# Revit family: HeartFelt-Linear-Endcap Panel1_HunterDouglasEurope
name_source: partatom
category: Specialty Equipment
revit_build: Autodesk Revit 2016 (Build: 20150220_1215(x64)
units: mm (PartAtom-declared; Revit-internal decimal feet)

## family parameters
Always vertical = Yes
Cut with Voids When Loaded = No
OmniClass Number = 23.35.70.24.11.17.14
OmniClass Title = Linear Ceilings
Part Type = Normal
Room Calculation Point = No
Round Connector Dimension = Use Diameter
Shared = No
Work Plane-Based = No

## types (36) — shared parameters
EN13501-1_Fire rating = Class B,s1,d0
Manufacturer = Hunter Douglas
Product Data = http://assets2.hunterdouglascontract.com
Product Line = HeartFelt® Linear
Subcategory = HeartFelt® Ceilings
Thickness = 6 mm  [stored 0.019685 ft]
URL = http://www.hunterdouglasarchitectural.eu

## per-type parameters (varying)
| type | Article Code | Colour Code | Height | Material | Model |
| Endcap Panel1_40x55_7575 Creme | 38.4208 | 7575 | 51.5 mm  [stored 0.168963 ft] | HeartFelt-7575-Creme_HunterDouglasEurope | HeartFelt EndcapPanel1 40x55 |
| Endcap Panel1_40x55_7576 Light Brown | 38.4208 | 7576 | 51.5 mm  [stored 0.168963 ft] | HeartFelt-7576-Light Brown_HunterDouglasEurope | HeartFelt EndcapPanel1 40x55 |
| Endcap Panel1_40x55_7577 Medium Brown | 38.4208 | 7577 | 51.5 mm  [stored 0.168963 ft] | HeartFelt-7577-Medium Brown_HunterDouglasEurope | HeartFelt EndcapPanel1 40x55 |
| Endcap Panel1_40x55_7578 Dark Brown | 38.4208 | 7578 | 51.5 mm  [stored 0.168963 ft] | HeartFelt-7578-Dark Brown_HunterDouglasEurope | HeartFelt EndcapPanel1 40x55 |
| Endcap Panel1_40x55_7579 Umber | 38.4208 | 7579 | 51.5 mm  [stored 0.168963 ft] | HeartFelt-7579-Umber_HunterDouglasEurope | HeartFelt EndcapPanel1 40x55 |
| Endcap Panel1_40x55_7593 White | 38.4208 | 7593 | 51.5 mm  [stored 0.168963 ft] | HeartFelt-7593-White_HunterDouglasEurope | HeartFelt EndcapPanel1 40x55 |
| Endcap Panel1_40x55_7594 Black | 38.4208 | 7594 | 51.5 mm  [stored 0.168963 ft] | HeartFelt-7594-Black_HunterDouglasEurope | HeartFelt EndcapPanel1 40x55 |
| Endcap Panel1_40x55_7595 Off White | 38.4208 | 7595 | 51.5 mm  [stored 0.168963 ft] | HeartFelt-7595-Off White_HunterDouglasEurope | HeartFelt EndcapPanel1 40x55 |
| Endcap Panel1_40x55_7596 Light Grey | 38.4208 | 7596 | 51.5 mm  [stored 0.168963 ft] | HeartFelt-7596-Light Grey_HunterDouglasEurope | HeartFelt EndcapPanel1 40x55 |
| Endcap Panel1_40x55_7597 Middle Grey | 38.4208 | 7597 | 51.5 mm  [stored 0.168963 ft] | HeartFelt-7597-Middle Grey_HunterDouglasEurope | HeartFelt EndcapPanel1 40x55 |
| Endcap Panel1_40x55_7598 Dark Grey | 38.4208 | 7598 | 51.5 mm  [stored 0.168963 ft] | HeartFelt-7598-Dark Grey_HunterDouglasEurope | HeartFelt EndcapPanel1 40x55 |
| Endcap Panel1_40x55_7599 Anthracite | 38.4208 | 7599 | 51.5 mm  [stored 0.168963 ft] | HeartFelt-7599-Anthracite_HunterDouglasEurope | HeartFelt EndcapPanel1 40x55 |
| Endcap Panel1_40x80_7575 Creme | 38.4209 | 7575 | 76.5 mm | HeartFelt-7575-Creme_HunterDouglasEurope | HeartFelt EndcapPanel1 40x80 |
| Endcap Panel1_40x80_7576 Light Brown | 38.4209 | 7576 | 76.5 mm | HeartFelt-7576-Light Brown_HunterDouglasEurope | HeartFelt EndcapPanel1 40x80 |
| Endcap Panel1_40x80_7577 Medium Brown | 38.4209 | 7577 | 76.5 mm | HeartFelt-7577-Medium Brown_HunterDouglasEurope | HeartFelt EndcapPanel1 40x80 |
| Endcap Panel1_40x80_7578 Dark Brown | 38.4209 | 7578 | 76.5 mm | HeartFelt-7578-Dark Brown_HunterDouglasEurope | HeartFelt EndcapPanel1 40x80 |
| Endcap Panel1_40x80_7579 Umber | 38.4209 | 7579 | 76.5 mm | HeartFelt-7579-Umber_HunterDouglasEurope | HeartFelt EndcapPanel1 40x80 |
| Endcap Panel1_40x80_7593 White | 38.4209 | 7593 | 76.5 mm | HeartFelt-7593-White_HunterDouglasEurope | HeartFelt EndcapPanel1 40x80 |
| Endcap Panel1_40x80_7594 Black | 38.4209 | 7594 | 76.5 mm | HeartFelt-7594-Black_HunterDouglasEurope | HeartFelt EndcapPanel1 40x80 |
| Endcap Panel1_40x80_7595 Off White | 38.4209 | 7595 | 76.5 mm | HeartFelt-7595-Off White_HunterDouglasEurope | HeartFelt EndcapPanel1 40x80 |
| Endcap Panel1_40x80_7596 Light Grey | 38.4209 | 7596 | 76.5 mm | HeartFelt-7596-Light Grey_HunterDouglasEurope | HeartFelt EndcapPanel1 40x80 |
| Endcap Panel1_40x80_7597 Middle Grey | 38.4209 | 7597 | 76.5 mm | HeartFelt-7597-Middle Grey_HunterDouglasEurope | HeartFelt EndcapPanel1 40x80 |
| Endcap Panel1_40x80_7598 Dark Grey | 38.4209 | 7598 | 76.5 mm | HeartFelt-7598-Dark Grey_HunterDouglasEurope | HeartFelt EndcapPanel1 40x80 |
| Endcap Panel1_40x80_7599 Anthracite | 38.4209 | 7599 | 76.5 mm | HeartFelt-7599-Anthracite_HunterDouglasEurope | HeartFelt EndcapPanel1 40x80 |
| Endcap Panel1_40x105_7575 Creme | 38.4210 | 7575 | 101.5 mm | HeartFelt-7575-Creme_HunterDouglasEurope | HeartFelt EndcapPanel1 40x105 |
| Endcap Panel1_40x105_7576 Light Brown | 38.4210 | 7576 | 101.5 mm | HeartFelt-7576-Light Brown_HunterDouglasEurope | HeartFelt EndcapPanel1 40x105 |
| Endcap Panel1_40x105_7577 Medium Brown | 38.4210 | 7577 | 101.5 mm | HeartFelt-7577-Medium Brown_HunterDouglasEurope | HeartFelt EndcapPanel1 40x105 |
| Endcap Panel1_40x105_7578 Dark Brown | 38.4210 | 7578 | 101.5 mm | HeartFelt-7578-Dark Brown_HunterDouglasEurope | HeartFelt EndcapPanel1 40x105 |
| Endcap Panel1_40x105_7579 Umber | 38.4210 | 7579 | 101.5 mm | HeartFelt-7579-Umber_HunterDouglasEurope | HeartFelt EndcapPanel1 40x105 |
| Endcap Panel1_40x105_7593 White | 38.4210 | 7593 | 101.5 mm | HeartFelt-7593-White_HunterDouglasEurope | HeartFelt EndcapPanel1 40x105 |
| Endcap Panel1_40x105_7594 Black | 38.4210 | 7594 | 101.5 mm | HeartFelt-7594-Black_HunterDouglasEurope | HeartFelt EndcapPanel1 40x105 |
| Endcap Panel1_40x105_7595 Off White | 38.4210 | 7595 | 101.5 mm | HeartFelt-7595-Off White_HunterDouglasEurope | HeartFelt EndcapPanel1 40x105 |
| Endcap Panel1_40x105_7596 Light Grey | 38.4210 | 7596 | 101.5 mm | HeartFelt-7596-Light Grey_HunterDouglasEurope | HeartFelt EndcapPanel1 40x105 |
| Endcap Panel1_40x105_7597 Middle Grey | 38.4210 | 7597 | 101.5 mm | HeartFelt-7597-Middle Grey_HunterDouglasEurope | HeartFelt EndcapPanel1 40x105 |
| Endcap Panel1_40x105_7598 Dark Grey | 38.4210 | 7598 | 101.5 mm | HeartFelt-7598-Dark Grey_HunterDouglasEurope | HeartFelt EndcapPanel1 40x105 |
| Endcap Panel1_40x105_7599 Anthracite | 38.4210 | 7599 | 101.5 mm | HeartFelt-7599-Anthracite_HunterDouglasEurope | HeartFelt EndcapPanel1 40x105 |

note: [stored X ft] marks values corroborated as IEEE doubles in the binary element streams (Revit-internal decimal feet)

## geometry (parser evidence)
native form markers: Sweep x3
no freeform markers — native parametric forms only
